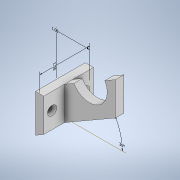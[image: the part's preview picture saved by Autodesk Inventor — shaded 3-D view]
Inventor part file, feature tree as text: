
AUTODESK INVENTOR PART (.ipt)
format: ipt  version: 2021.1 (Build 251245000, 245)  size: 156,160 bytes
history: native  units: in
note: dims shown in document units (in); Inventor stores cm internally (conversion verified against a paired STEP export)
features: other x4, sketch x4, extrude x3, hole x1
ambient origin geometry x8: Origin, YZ Plane, XZ Plane, XY Plane, X Axis, Y Axis, Z Axis, Center Point
bodies: Solid2 (feature_tree)
feature tree (12):
  other  "Annotations"
  extrude  "Extrusion3"  Depth=0.25in
  extrude  "Extrusion4"  TaperAngle=30.0deg  [1 undecoded]
  sketch  "Sketch7"  dims[d26=1.075in d29=0.25in]
  extrude  "Extrusion5"  Depth=0.25in
  hole  "Hole3"  [1 undecoded]
  sketch  "Sketch5"  dims[d21=1.0in d22=0.25in]
  sketch  "Sketch6"  dims[d23=1.5in d24=0.0in d25=30.0deg]
  sketch  "Sketch8"  dims[d30=1.0in d31=0.25in d32=0.0in d33=0.0in d34=0.25in d35=0.25in d47=1.5in d48=0.0in d49=0.15in d50=0.75in d51=0.279in d52=0.25in d53=0.5635in d54=1.0in d55=0.8108in d56=0.2085in d57=0.331in d58=1.5in d59=2.3174in d60=30.0deg d62=1.0in]
  other  "Linear Dimension 1"
  other  "Angular Dimension 1"
  other  "Linear Dimension 3"
note: 2 required parameter values undecoded (feature->parameter linkage not recoverable at this tier; creation-order binding heuristic only, values carry confidence <= 0.55)
